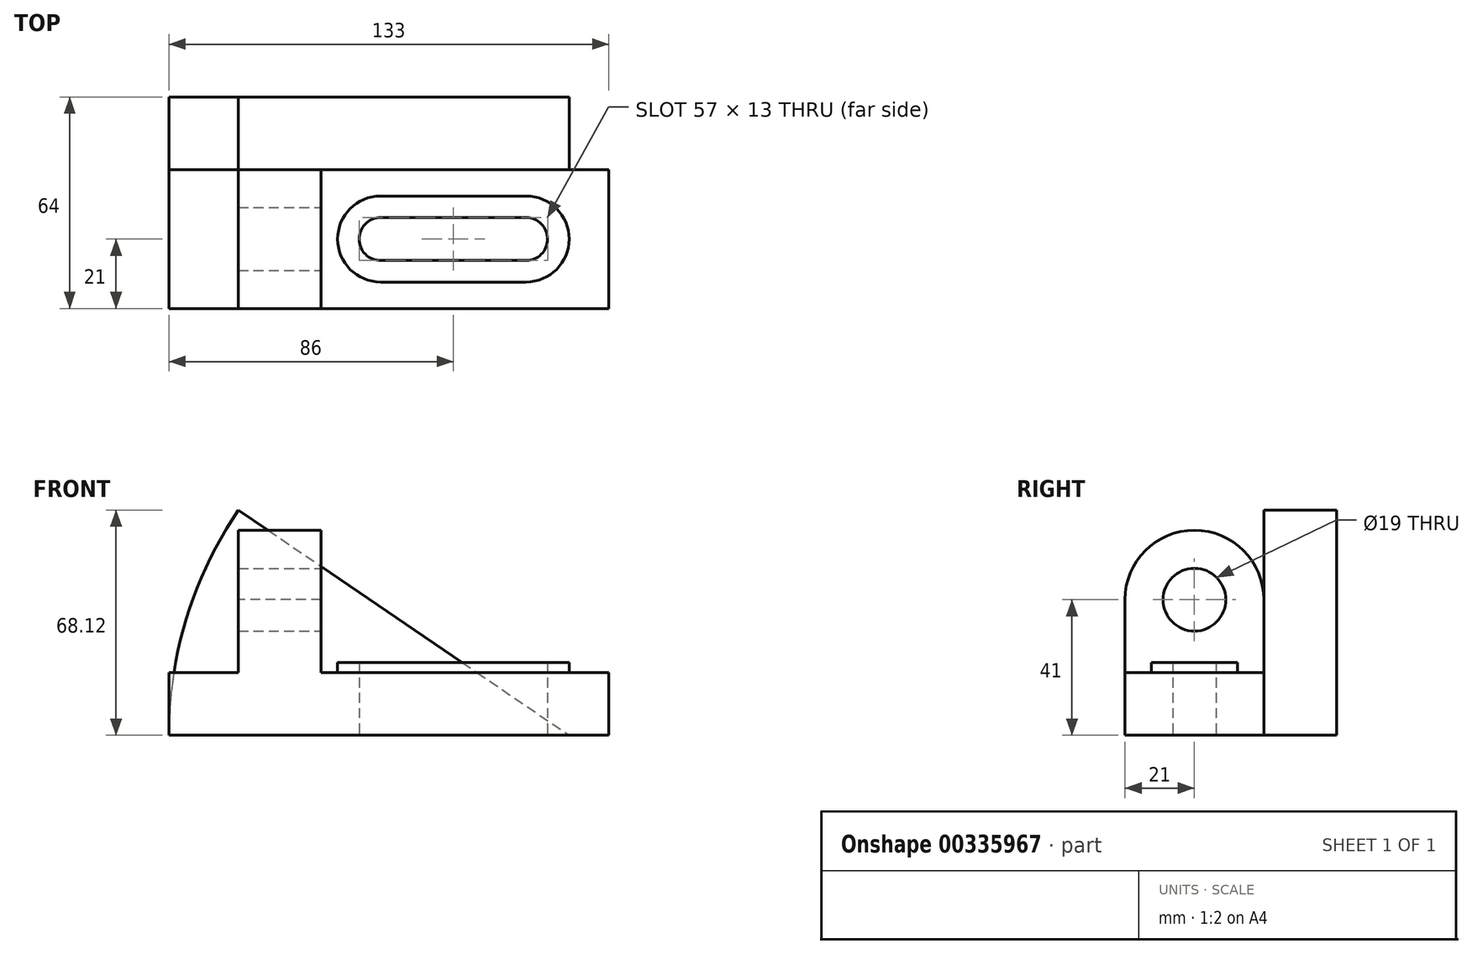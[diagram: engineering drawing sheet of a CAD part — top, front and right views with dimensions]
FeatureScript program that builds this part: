
annotation { "Feature Type Name" : "Feature", "Feature Type Description" : "" }
export const myFeature = defineFeature(function(context is Context, id is Id, definition is map)
    precondition{}
    {
        {
            var Q0;
            Q0=qCreatedBy(makeId("Right.planeOp"),FACE);
            var sketch = newSketch(context, id + "F0", { "sketchPlane" : qUnion([Q0])});
            skLineSegment(sketch, "E0", {"start": v(0, 0) * mm, "end": v(42, 0) * mm});
            skLineSegment(sketch, "E1", {"start": v(42, 0) * mm, "end": v(42, 19) * mm});
            skLineSegment(sketch, "E2", {"start": v(42, 19) * mm, "end": v(0, 19) * mm});
            skLineSegment(sketch, "E3", {"start": v(0, 19) * mm, "end": v(0, 0) * mm});
            skLineSegment(sketch, "E4", {"start": v(0, 19) * mm, "end": v(0, 41) * mm});
            skLineSegment(sketch, "E5", {"start": v(42, 19) * mm, "end": v(42, 41) * mm});
            skArc(sketch, "E6", {"start": v(42, 41) * mm, "mid": v(21, 62) * mm, "end": v(0, 41) * mm});
            skSolve(sketch);
        }
        {
            var Q0;
            Q0=makeQuery(id+"F0.imprint","IMPRINT",FACE,{"disambiguationData":[TD([[makeQuery(id+"F0.imprint","IMPRINT",EDGE,{"derivedFrom":sQuery(id+"F0.wireOp",EDGE,"E0")}),1.0]])]});
            extrude(context, id + "F1", {"entities" : qUnion([Q0]), "depth" : 133 * mm});
        }
        {
            var Q0;
            Q0=makeQuery(id+"F0.imprint","IMPRINT",FACE,{"disambiguationData":[TD([[makeQuery(id+"F0.imprint","IMPRINT",EDGE,{"derivedFrom":sQuery(id+"F0.wireOp",EDGE,"E2")}),-1.0]])]});
            extrude(context, id + "F2", {"entities" : qUnion([Q0]), "operationType" : NewBodyOperationType.ADD, "depth" : 25 * mm});
        }
        {
            var Q0;
            Q0=makeQuery(id+"F1.opExtrude","SWEPT_FACE",FACE,{"disambiguationData":[OSD([sQuery(id+"F0.wireOp",EDGE,"E2")])]});
            var sketch = newSketch(context, id + "F3", { "sketchPlane" : qUnion([Q0])});
            skLineSegment(sketch, "E7", {"start": v(25, 0) * mm, "end": v(25, 42) * mm});
            skLineSegment(sketch, "E8.bottom", {"start": v(0, 42) * mm, "end": v(25, 42) * mm});
            skLineSegment(sketch, "E8.top", {"start": v(0, 0) * mm, "end": v(25, 0) * mm});
            skLineSegment(sketch, "E8.left", {"start": v(0, 42) * mm, "end": v(0, 0) * mm});
            skLineSegment(sketch, "E9.bottom", {"start": v(0, 42) * mm, "end": v(-21, 42) * mm});
            skLineSegment(sketch, "E9.top", {"start": v(0, 0) * mm, "end": v(-21, 0) * mm});
            skLineSegment(sketch, "E9.right", {"start": v(-21, 42) * mm, "end": v(-21, 0) * mm});
            skSolve(sketch);
        }
        {
            var Q0;
            Q0=makeQuery(id+"F3.imprint","IMPRINT",FACE,{"disambiguationData":[TD([[makeQuery(id+"F3.imprint","IMPRINT",EDGE,{"derivedFrom":sQuery(id+"F3.wireOp",EDGE,"E9.bottom")}),1.0]])]});
            extrude(context, id + "F4", {"entities" : qUnion([Q0]), "operationType" : NewBodyOperationType.ADD, "oppositeDirection" : true, "depth" : 19 * mm});
        }
        {
            var Q0;
            Q0=makeQuery(id+"F2.opExtrude","CAP_FACE",FACE,{"disambiguationData":[OSD([sQuery(id+"F0.wireOp",EDGE,"E2"),sQuery(id+"F0.wireOp",EDGE,"E4"),sQuery(id+"F0.wireOp",EDGE,"E5"),sQuery(id+"F0.wireOp",EDGE,"E6")])],"isStart":false});
            var sketch = newSketch(context, id + "F5", { "sketchPlane" : qUnion([Q0])});
            skCircle(sketch, "E10", {"center": v(21, 41) * mm, "radius": 9.5 * mm});
            skSolve(sketch);
        }
        {
            var Q0;
            Q0=makeQuery(id+"F5.imprint","IMPRINT",FACE,{"disambiguationData":[TD([[makeQuery(id+"F5.imprint","IMPRINT",EDGE,{"derivedFrom":sQuery(id+"F5.wireOp",EDGE,"E10")}),1.0]])]});
            extrude(context, id + "F6", {"entities" : qUnion([Q0]), "operationType" : NewBodyOperationType.REMOVE, "endBound" : BoundingType.THROUGH_ALL, "oppositeDirection" : true, "depth" : 25 * mm});
        }
        {
            var Q0;
            Q0=makeQuery(id+"F1.opExtrude","SWEPT_FACE",FACE,{"disambiguationData":[OSD([sQuery(id+"F0.wireOp",EDGE,"E2")])]});
            var sketch = newSketch(context, id + "F7", { "sketchPlane" : qUnion([Q0])});
            skLineSegment(sketch, "E11", {"start": v(112, 42) * mm, "end": v(112, 0) * mm});
            skLineSegment(sketch, "E12", {"start": v(112, 0) * mm, "end": v(133, 0) * mm});
            skLineSegment(sketch, "E13", {"start": v(133, 0) * mm, "end": v(133, 42) * mm});
            skLineSegment(sketch, "E14", {"start": v(133, 42) * mm, "end": v(112, 42) * mm});
            skSolve(sketch);
        }
        {
            var Q0;
            Q0=makeQuery(id+"F7.imprint","IMPRINT",FACE,{"disambiguationData":[TD([[makeQuery(id+"F7.imprint","IMPRINT",EDGE,{"derivedFrom":sQuery(id+"F7.wireOp",EDGE,"E11")}),1.0]])]});
            extrude(context, id + "F8", {"entities" : qUnion([Q0]), "operationType" : NewBodyOperationType.REMOVE, "endBound" : BoundingType.THROUGH_ALL, "oppositeDirection" : true, "depth" : 25 * mm});
        }
        {
            var Q0;
            Q0=makeQuery(id+"F1.opExtrude","SWEPT_FACE",FACE,{"disambiguationData":[OSD([sQuery(id+"F0.wireOp",EDGE,"E2")])]});
            var sketch = newSketch(context, id + "F9", { "sketchPlane" : qUnion([Q0])});
            skLineSegment(sketch, "E15", {"start": v(43, 27.5) * mm, "end": v(87, 27.5) * mm});
            skLineSegment(sketch, "E16", {"start": v(43, 14.5) * mm, "end": v(87, 14.5) * mm});
            skArc(sketch, "E17", {"start": v(43, 27.5) * mm, "mid": v(36.5, 21) * mm, "end": v(43, 14.5) * mm});
            skArc(sketch, "E18", {"start": v(87, 14.5) * mm, "mid": v(93.5, 21) * mm, "end": v(87, 27.5) * mm});
            skLineSegment(sketch, "E19", {"start": v(43, 34) * mm, "end": v(87, 34) * mm});
            skLineSegment(sketch, "E20", {"start": v(87, 8) * mm, "end": v(43, 8) * mm});
            skArc(sketch, "E21", {"start": v(43, 34) * mm, "mid": v(30, 21) * mm, "end": v(43, 8) * mm});
            skArc(sketch, "E22", {"start": v(87, 8) * mm, "mid": v(100, 21) * mm, "end": v(87, 34) * mm});
            skSolve(sketch);
        }
        {
            var Q0;
            Q0=makeQuery(id+"F9.imprint","IMPRINT",FACE,{"disambiguationData":[TD([[makeQuery(id+"F9.imprint","IMPRINT",EDGE,{"derivedFrom":sQuery(id+"F9.wireOp",EDGE,"E15")}),1.0]])]});
            extrude(context, id + "F10", {"entities" : qUnion([Q0]), "operationType" : NewBodyOperationType.ADD, "depth" : 3 * mm});
        }
        {
            var Q0;
            Q0=makeQuery(id+"F9.imprint","IMPRINT",FACE,{"disambiguationData":[TD([[makeQuery(id+"F9.imprint","IMPRINT",EDGE,{"derivedFrom":sQuery(id+"F9.wireOp",EDGE,"E15")}),-1.0]])]});
            extrude(context, id + "F11", {"entities" : qUnion([Q0]), "operationType" : NewBodyOperationType.REMOVE, "endBound" : BoundingType.THROUGH_ALL, "oppositeDirection" : true, "depth" : 25 * mm});
        }
        {
            var Q0;
            Q0=makeQuery(id+"F4.boolean.opBoolean","MERGE",FACE,{"derivedFrom":[makeQuery(id+"F2.boolean.opBoolean","MERGE",FACE,{"derivedFrom":[makeQuery(id+"F1.opExtrude","SWEPT_FACE",FACE,{"disambiguationData":[OSD([sQuery(id+"F0.wireOp",EDGE,"E1")])]}),makeQuery(id+"F2.opExtrude","SWEPT_FACE",FACE,{"disambiguationData":[OSD([sQuery(id+"F0.wireOp",EDGE,"E5")])]})]}),makeQuery(id+"F4.opExtrude","SWEPT_FACE",FACE,{"disambiguationData":[OSD([sQuery(id+"F3.wireOp",EDGE,"E9.bottom")])]})]});
            var sketch = newSketch(context, id + "F12", { "sketchPlane" : qUnion([Q0])});
            skArc(sketch, "E23", {"start": v(21, 0) * mm, "mid": v(15.63, 35.64) * mm, "end": v(0, 68.12) * mm});
            skLineSegment(sketch, "E24", {"start": v(0, 68.12) * mm, "end": v(-100, 0) * mm});
            skLineSegment(sketch, "E25", {"start": v(21, 0) * mm, "end": v(-100, 0) * mm});
            skSolve(sketch);
        }
        {
            var Q0;
            Q0 = qSketchRegion(id + "F12", true);
            extrude(context, id + "F13", {"entities" : qUnion([Q0]), "operationType" : NewBodyOperationType.ADD, "depth" : 22 * mm});
        }
    });
